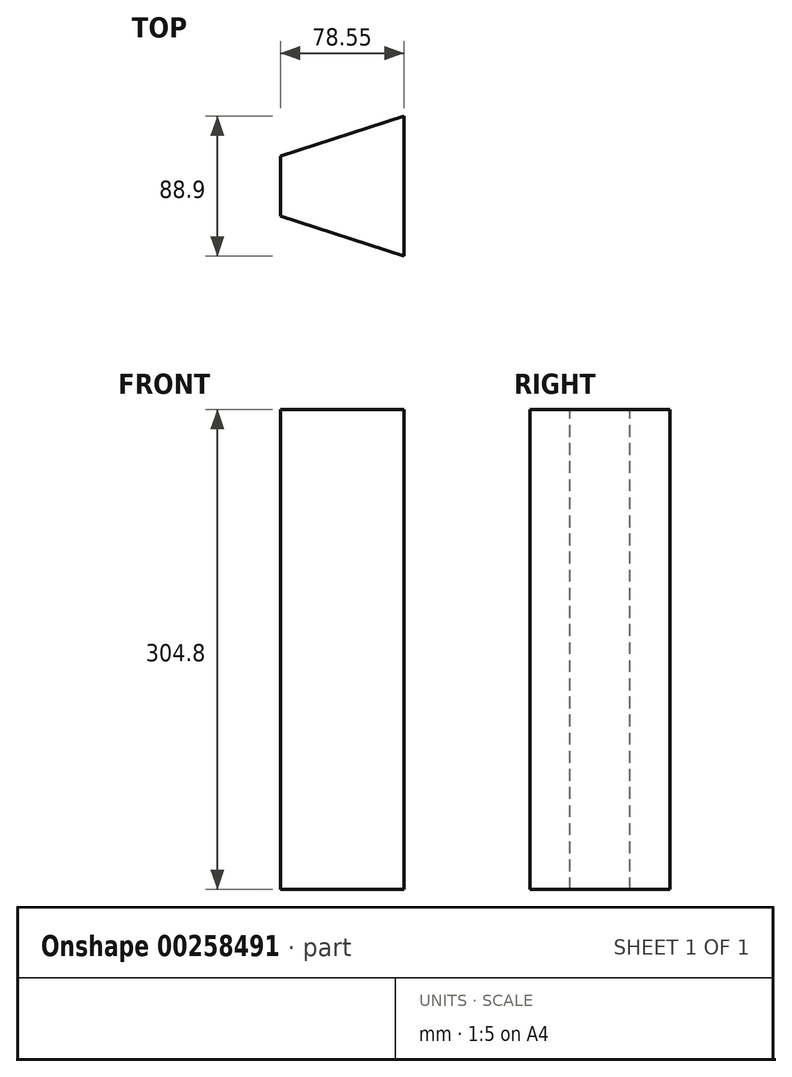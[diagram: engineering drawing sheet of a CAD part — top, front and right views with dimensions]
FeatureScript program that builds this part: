
annotation { "Feature Type Name" : "Feature", "Feature Type Description" : "" }
export const myFeature = defineFeature(function(context is Context, id is Id, definition is map)
    precondition{}
    {
        {
            var Q0;
            Q0=qCreatedBy(makeId("Top.planeOp"),FACE);
            var sketch = newSketch(context, id + "F0", { "sketchPlane" : qUnion([Q0])});
            skLineSegment(sketch, "E0", {"start": v(0, 0) * mm, "end": v(0, 44.45) * mm});
            skLineSegment(sketch, "E1", {"start": v(-78.55, 0) * mm, "end": v(-78.55, 19.05) * mm});
            skLineSegment(sketch, "E2", {"start": v(-78.55, 19.05) * mm, "end": v(0, 44.45) * mm});
            skLineSegment(sketch, "E3.MirrorCS", {"start": v(-78.55, 0) * mm, "end": v(-78.55, -19.05) * mm});
            skLineSegment(sketch, "E4.MirrorCS", {"start": v(-78.55, -19.05) * mm, "end": v(0, -44.45) * mm});
            skLineSegment(sketch, "E5.MirrorCS", {"start": v(0, 0) * mm, "end": v(0, -44.45) * mm});
            skSolve(sketch);
        }
        {
            var Q0;
            Q0=makeQuery(id+"F0.imprint","IMPRINT",FACE,{"disambiguationData":[TD([[makeQuery(id+"F0.imprint","IMPRINT",EDGE,{"derivedFrom":sQuery(id+"F0.wireOp",EDGE,"E0")}),1.0]])]});
            extrude(context, id + "F1", {"entities" : qUnion([Q0]), "oppositeDirection" : true, "depth" : 304.8 * mm});
        }
        {
            var Q0;
            Q0=makeQuery(id+"F1.opExtrude","SWEPT_FACE",FACE,{"disambiguationData":[OSD([sQuery(id+"F0.wireOp",EDGE,"E1"),sQuery(id+"F0.wireOp",EDGE,"E3.MirrorCS")])]});
            var sketch = newSketch(context, id + "F2", { "sketchPlane" : qUnion([Q0])});
            skLineSegment(sketch, "E6.bottom", {"start": v(-19.05, 0) * mm, "end": v(19.05, 0) * mm});
            skLineSegment(sketch, "E6.top", {"start": v(-19.05, -203.2) * mm, "end": v(19.05, -203.2) * mm});
            skLineSegment(sketch, "E6.left", {"start": v(-19.05, 0) * mm, "end": v(-19.05, -203.2) * mm});
            skLineSegment(sketch, "E6.right", {"start": v(19.05, 0) * mm, "end": v(19.05, -203.2) * mm});
            skSolve(sketch);
        }
    });
